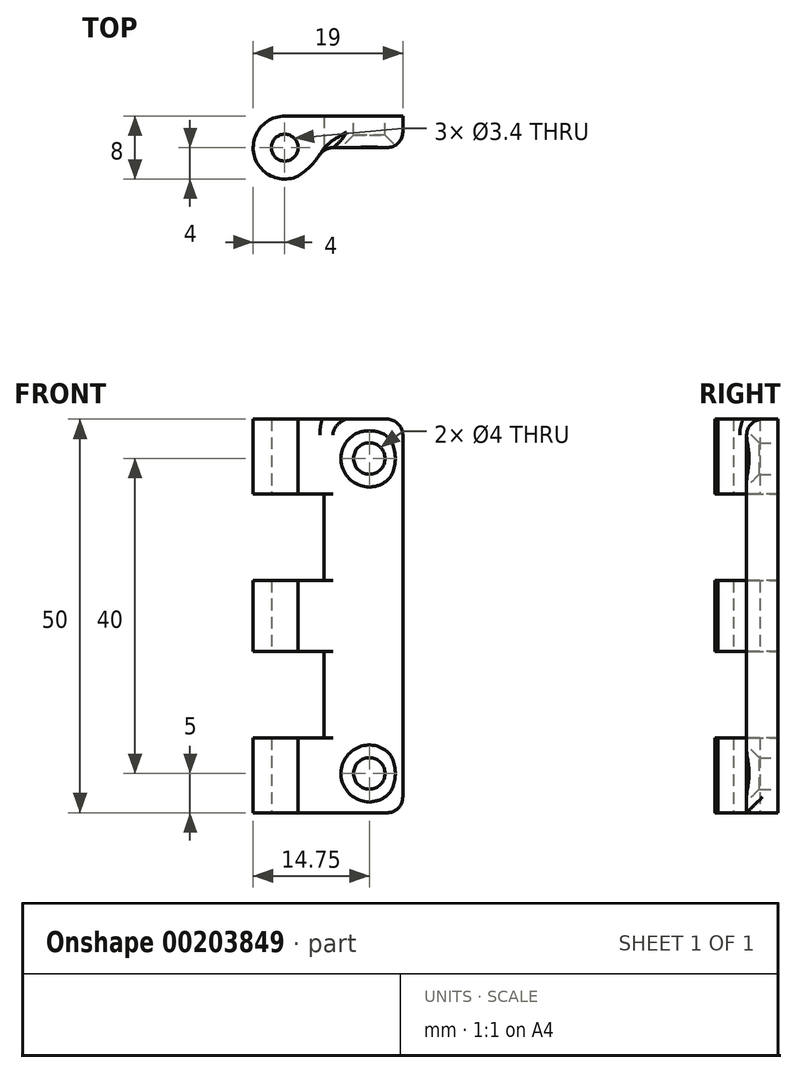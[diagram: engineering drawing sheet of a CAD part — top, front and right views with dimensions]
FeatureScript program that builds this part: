
annotation { "Feature Type Name" : "Feature", "Feature Type Description" : "" }
export const myFeature = defineFeature(function(context is Context, id is Id, definition is map)
    precondition{}
    {
        {
            var Q0;
            Q0=qCreatedBy(makeId("Front.planeOp"),FACE);
            var sketch = newSketch(context, id + "F0", { "sketchPlane" : qUnion([Q0])});
            skLineSegment(sketch, "E0", {"start": v(0, -25) * mm, "end": v(0, 25) * mm});
            skLineSegment(sketch, "E1", {"start": v(0, 25) * mm, "end": v(15, 25) * mm});
            skLineSegment(sketch, "E2", {"start": v(15, 25) * mm, "end": v(15, -25) * mm});
            skLineSegment(sketch, "E3", {"start": v(15, -25) * mm, "end": v(0, -25) * mm});
            skCircle(sketch, "E4", {"center": v(10.75, 20) * mm, "radius": 2 * mm});
            skCircle(sketch, "E5", {"center": v(10.75, -20) * mm, "radius": 2 * mm});
            skLineSegment(sketch, "E6", {"start": v(10.75, -20) * mm, "end": v(10.75, 20) * mm, "construction": true});
            skSolve(sketch);
        }
        {
            var Q0;
            Q0 = qSketchRegion(id + "F0", true);
            extrude(context, id + "F1", {"entities" : qUnion([Q0]), "endBound" : BoundingType.SYMMETRIC, "depth" : 4 * mm});
        }
        {
            var Q0;
            Q0=makeQuery(id+"F1.opExtrude","SWEPT_FACE",FACE,{"disambiguationData":[OSD([sQuery(id+"F0.wireOp",EDGE,"E3")])]});
            var sketch = newSketch(context, id + "F2", { "sketchPlane" : qUnion([Q0])});
            skArc(sketch, "E7", {"start": v(2, 5.46) * mm, "mid": v(-3.46, 0) * mm, "end": v(4, 2) * mm});
            skLineSegment(sketch, "E8", {"start": v(2, 5.46) * mm, "end": v(8, 2) * mm});
            skLineSegment(sketch, "E9", {"start": v(8, 2) * mm, "end": v(4, 2) * mm});
            skSolve(sketch);
        }
        {
            var Q0;
            Q0 = qSketchRegion(id + "F2", true);
            extrude(context, id + "F3", {"entities" : qUnion([Q0]), "operationType" : NewBodyOperationType.ADD, "oppositeDirection" : true, "depth" : 50 * mm});
        }
        {
            var Q0;
            Q0=makeQuery(id+"F3.boolean.opBoolean","MERGE",FACE,{"derivedFrom":[makeQuery(id+"F1.opExtrude","SWEPT_FACE",FACE,{"disambiguationData":[OSD([sQuery(id+"F0.wireOp",EDGE,"E3")])]}),makeQuery(id+"F3.opExtrude","CAP_FACE",FACE,{"disambiguationData":[OSD([sQuery(id+"F2.wireOp",EDGE,"E7"),sQuery(id+"F2.wireOp",EDGE,"E8"),sQuery(id+"F2.wireOp",EDGE,"E9")])],"isStart":true})]});
            var sketch = newSketch(context, id + "F4", { "sketchPlane" : qUnion([Q0])});
            skLineSegment(sketch, "E10.bottom", {"start": v(15, 2) * mm, "end": v(5, 2) * mm});
            skLineSegment(sketch, "E10.top", {"start": v(15, 4) * mm, "end": v(5, 4) * mm});
            skLineSegment(sketch, "E10.left", {"start": v(15, 2) * mm, "end": v(15, 4) * mm});
            skLineSegment(sketch, "E10.right", {"start": v(5, 2) * mm, "end": v(5, 4) * mm});
            skSolve(sketch);
        }
        {
            var Q0;
            Q0 = qSketchRegion(id + "F4", true);
            extrude(context, id + "F5", {"entities" : qUnion([Q0]), "operationType" : NewBodyOperationType.REMOVE, "endBound" : BoundingType.THROUGH_ALL, "oppositeDirection" : true, "depth" : 25 * mm});
        }
        {
            var Q0;
            Q0=makeQuery(id+"F5.boolean.opBoolean","MERGE",FACE,{"derivedFrom":[makeQuery(id+"F1.opExtrude","CAP_FACE",FACE,{"disambiguationData":[OSD([sQuery(id+"F0.wireOp",EDGE,"E0"),sQuery(id+"F0.wireOp",EDGE,"E1"),sQuery(id+"F0.wireOp",EDGE,"E2"),sQuery(id+"F0.wireOp",EDGE,"E3")])],"isStart":false}),makeQuery(id+"F5.opExtrude","SWEPT_FACE",FACE,{"disambiguationData":[OSD([sQuery(id+"F4.wireOp",EDGE,"E10.bottom")])]})]});
            var sketch = newSketch(context, id + "F6", { "sketchPlane" : qUnion([Q0])});
            skLineSegment(sketch, "E11.bottom", {"start": v(-5, 15.5) * mm, "end": v(5, 15.5) * mm});
            skLineSegment(sketch, "E11.top", {"start": v(-5, 4.5) * mm, "end": v(5, 4.5) * mm});
            skLineSegment(sketch, "E11.left", {"start": v(-5, 15.5) * mm, "end": v(-5, 4.5) * mm});
            skLineSegment(sketch, "E11.right", {"start": v(5, 15.5) * mm, "end": v(5, 4.5) * mm});
            skLineSegment(sketch, "E12.bottom", {"start": v(-5, -4.5) * mm, "end": v(5, -4.5) * mm});
            skLineSegment(sketch, "E12.top", {"start": v(-5, -15.5) * mm, "end": v(5, -15.5) * mm});
            skLineSegment(sketch, "E12.left", {"start": v(-5, -4.5) * mm, "end": v(-5, -15.5) * mm});
            skLineSegment(sketch, "E12.right", {"start": v(5, -4.5) * mm, "end": v(5, -15.5) * mm});
            skSolve(sketch);
        }
        {
            var Q0;
            Q0 = qSketchRegion(id + "F6", true);
            extrude(context, id + "F7", {"entities" : qUnion([Q0]), "operationType" : NewBodyOperationType.REMOVE, "endBound" : BoundingType.SYMMETRIC, "oppositeDirection" : true, "depth" : 25 * mm});
        }
        {
            var Q0;
            {var subQ0=makeQuery(id+"F5.opExtrude","SWEPT_FACE",FACE,{"disambiguationData":[OSD([sQuery(id+"F4.wireOp",EDGE,"E10.right")])]});var subQ1=sQuery(id+"F2.wireOp",EDGE,"E8");var subQ2=makeQuery(id+"F3.opExtrude","SWEPT_FACE",FACE,{"disambiguationData":[OSD([subQ1])]});Q0=makeQuery(id+"F7.boolean.opBoolean","SPLIT",EDGE,{"disambiguationData":[TD([makeQuery(id+"F1.opExtrude","SWEPT_FACE",FACE,{"disambiguationData":[OSD([sQuery(id+"F0.wireOp",EDGE,"E3")])]})])],"derivedFrom":makeQuery(id+"F5.boolean.opBoolean","INTERSECT",EDGE,{"derivedFrom":[subQ2,subQ0]})});}
            var Q1;
            {var subQ0=makeQuery(id+"F3.opExtrude","SWEPT_FACE",FACE,{"disambiguationData":[OSD([sQuery(id+"F2.wireOp",EDGE,"E8")])]});var subQ1=makeQuery(id+"F5.opExtrude","SWEPT_FACE",FACE,{"disambiguationData":[OSD([sQuery(id+"F4.wireOp",EDGE,"E10.right")])]});Q1=makeQuery(id+"F7.boolean.opBoolean","SPLIT",EDGE,{"disambiguationData":[TD([makeQuery(id+"F7.opExtrude","SWEPT_FACE",FACE,{"disambiguationData":[OSD([sQuery(id+"F6.wireOp",EDGE,"E11.top")])]})])],"derivedFrom":makeQuery(id+"F5.boolean.opBoolean","INTERSECT",EDGE,{"derivedFrom":[subQ0,subQ1]})});}
            var Q2;
            {var subQ0=makeQuery(id+"F5.opExtrude","SWEPT_FACE",FACE,{"disambiguationData":[OSD([sQuery(id+"F4.wireOp",EDGE,"E10.right")])]});var subQ1=sQuery(id+"F2.wireOp",EDGE,"E8");var subQ2=makeQuery(id+"F3.opExtrude","SWEPT_FACE",FACE,{"disambiguationData":[OSD([subQ1])]});Q2=makeQuery(id+"F7.boolean.opBoolean","SPLIT",EDGE,{"disambiguationData":[TD([makeQuery(id+"F1.opExtrude","SWEPT_FACE",FACE,{"disambiguationData":[OSD([sQuery(id+"F0.wireOp",EDGE,"E1")])]})])],"derivedFrom":makeQuery(id+"F5.boolean.opBoolean","INTERSECT",EDGE,{"derivedFrom":[subQ2,subQ0]})});}
            fillet(context, id + "F8", {"entities" : qUnion([Q0, Q1, Q2]), "radius" : 10 * mm, "tangentPropagation" : true, "allowEdgeOverflow" : false});
        }
        {
            var Q0;
            Q0=makeQuery(id+"F1.opExtrude","CAP_EDGE",EDGE,{"disambiguationData":[OSD([sQuery(id+"F0.wireOp",EDGE,"E2")])],"isStart":false});
            var Q1;
            Q1=makeQuery(id+"F5.boolean.opBoolean","INTERSECT",EDGE,{"derivedFrom":[makeQuery(id+"F3.boolean.opBoolean","MERGE",FACE,{"derivedFrom":[makeQuery(id+"F1.opExtrude","SWEPT_FACE",FACE,{"disambiguationData":[OSD([sQuery(id+"F0.wireOp",EDGE,"E1")])]}),makeQuery(id+"F3.opExtrude","CAP_FACE",FACE,{"disambiguationData":[OSD([sQuery(id+"F2.wireOp",EDGE,"E7"),sQuery(id+"F2.wireOp",EDGE,"E8"),sQuery(id+"F2.wireOp",EDGE,"E9")])],"isStart":false})]}),makeQuery(id+"F5.opExtrude","SWEPT_FACE",FACE,{"disambiguationData":[OSD([sQuery(id+"F4.wireOp",EDGE,"E10.bottom")])]})]});
            var Q2;
            {var subQ0=sQuery(id+"F4.wireOp",EDGE,"E10.right");var subQ1=sQuery(id+"F4.wireOp",EDGE,"E10.bottom");Q2=makeQuery(id+"F7.boolean.opBoolean","SPLIT",EDGE,{"disambiguationData":[TD([makeQuery(id+"F1.opExtrude","CAP_FACE",FACE,{"disambiguationData":[OSD([sQuery(id+"F0.wireOp",EDGE,"E0"),sQuery(id+"F0.wireOp",EDGE,"E1"),sQuery(id+"F0.wireOp",EDGE,"E2"),sQuery(id+"F0.wireOp",EDGE,"E3")])],"isStart":false}),makeQuery(id+"F5.opExtrude","SWEPT_FACE",FACE,{"disambiguationData":[OSD([subQ1])]}),makeQuery(id+"F5.boolean.opBoolean","COPY",FACE,{"derivedFrom":makeQuery(id+"F5.opExtrude","SWEPT_FACE",FACE,{"disambiguationData":[OSD([subQ0])]})}),makeQuery(id+"F7.opExtrude","SWEPT_FACE",FACE,{"disambiguationData":[OSD([sQuery(id+"F6.wireOp",EDGE,"E12.bottom")])]}),makeQuery(id+"F7.opExtrude","SWEPT_FACE",FACE,{"disambiguationData":[OSD([sQuery(id+"F6.wireOp",EDGE,"E12.top")])]}),makeQuery(id+"F7.opExtrude","SWEPT_FACE",FACE,{"disambiguationData":[OSD([sQuery(id+"F6.wireOp",EDGE,"E12.right")])]})])],"derivedFrom":makeQuery(id+"F5.boolean.opBoolean","COPY",EDGE,{"derivedFrom":makeQuery(id+"F5.opExtrude","SWEPT_EDGE",EDGE,{"disambiguationData":[OSD([subQ1,subQ0])]})})});}
            var Q3;
            {var subQ0=sQuery(id+"F4.wireOp",EDGE,"E10.right");var subQ1=sQuery(id+"F4.wireOp",EDGE,"E10.bottom");Q3=makeQuery(id+"F7.boolean.opBoolean","SPLIT",EDGE,{"disambiguationData":[TD([makeQuery(id+"F1.opExtrude","CAP_FACE",FACE,{"disambiguationData":[OSD([sQuery(id+"F0.wireOp",EDGE,"E0"),sQuery(id+"F0.wireOp",EDGE,"E1"),sQuery(id+"F0.wireOp",EDGE,"E2"),sQuery(id+"F0.wireOp",EDGE,"E3")])],"isStart":false}),makeQuery(id+"F5.opExtrude","SWEPT_FACE",FACE,{"disambiguationData":[OSD([subQ1])]}),makeQuery(id+"F5.boolean.opBoolean","COPY",FACE,{"derivedFrom":makeQuery(id+"F5.opExtrude","SWEPT_FACE",FACE,{"disambiguationData":[OSD([subQ0])]})}),makeQuery(id+"F7.opExtrude","SWEPT_FACE",FACE,{"disambiguationData":[OSD([sQuery(id+"F6.wireOp",EDGE,"E11.bottom")])]}),makeQuery(id+"F7.opExtrude","SWEPT_FACE",FACE,{"disambiguationData":[OSD([sQuery(id+"F6.wireOp",EDGE,"E11.top")])]}),makeQuery(id+"F7.opExtrude","SWEPT_FACE",FACE,{"disambiguationData":[OSD([sQuery(id+"F6.wireOp",EDGE,"E11.right")])]})])],"derivedFrom":makeQuery(id+"F5.boolean.opBoolean","COPY",EDGE,{"derivedFrom":makeQuery(id+"F5.opExtrude","SWEPT_EDGE",EDGE,{"disambiguationData":[OSD([subQ1,subQ0])]})})});}
            var Q4;
            Q4=makeQuery(id+"F5.boolean.opBoolean","MERGE",EDGE,{"derivedFrom":[makeQuery(id+"F1.opExtrude","CAP_EDGE",EDGE,{"disambiguationData":[OSD([sQuery(id+"F0.wireOp",EDGE,"E3")])],"isStart":false}),makeQuery(id+"F5.opExtrude","CAP_EDGE",EDGE,{"disambiguationData":[OSD([sQuery(id+"F4.wireOp",EDGE,"E10.bottom")])],"isStart":true})]});
            var Q5;
            Q5=makeQuery(id+"F1.opExtrude","SWEPT_EDGE",EDGE,{"disambiguationData":[OSD([sQuery(id+"F0.wireOp",EDGE,"E2"),sQuery(id+"F0.wireOp",EDGE,"E3")])]});
            var Q6;
            Q6=makeQuery(id+"F1.opExtrude","SWEPT_EDGE",EDGE,{"disambiguationData":[OSD([sQuery(id+"F0.wireOp",EDGE,"E1"),sQuery(id+"F0.wireOp",EDGE,"E2")])]});
            fillet(context, id + "F9", {"entities" : qUnion([Q0, Q1, Q2, Q3, Q4, Q5, Q6]), "radius" : 2 * mm, "tangentPropagation" : true, "allowEdgeOverflow" : false});
        }
        {
            var Q0;
            {var subQ0=sQuery(id+"F0.wireOp",EDGE,"E3");var subQ1=makeQuery(id+"F5.opExtrude","SWEPT_FACE",FACE,{"disambiguationData":[OSD([sQuery(id+"F4.wireOp",EDGE,"E10.right")])]});var subQ2=sQuery(id+"F2.wireOp",EDGE,"E8");var subQ3=makeQuery(id+"F3.opExtrude","SWEPT_FACE",FACE,{"disambiguationData":[OSD([subQ2])]});Q0=makeQuery(id+"F8.opFillet","BLEND_EDGE",EDGE,{"blendedFrom":[makeQuery(id+"F7.boolean.opBoolean","SPLIT",EDGE,{"disambiguationData":[TD([makeQuery(id+"F1.opExtrude","SWEPT_FACE",FACE,{"disambiguationData":[OSD([subQ0])]})])],"derivedFrom":makeQuery(id+"F5.boolean.opBoolean","INTERSECT",EDGE,{"derivedFrom":[subQ3,subQ1]})}),makeQuery(id+"F5.boolean.opBoolean","MERGE",FACE,{"derivedFrom":[makeQuery(id+"F1.opExtrude","CAP_FACE",FACE,{"disambiguationData":[OSD([sQuery(id+"F0.wireOp",EDGE,"E0"),sQuery(id+"F0.wireOp",EDGE,"E1"),sQuery(id+"F0.wireOp",EDGE,"E2"),subQ0])],"isStart":false}),makeQuery(id+"F5.opExtrude","SWEPT_FACE",FACE,{"disambiguationData":[OSD([sQuery(id+"F4.wireOp",EDGE,"E10.bottom")])]})]})],"blendedInto":[makeQuery(id+"F5.boolean.opBoolean","MERGE",FACE,{"derivedFrom":[makeQuery(id+"F1.opExtrude","CAP_FACE",FACE,{"disambiguationData":[OSD([sQuery(id+"F0.wireOp",EDGE,"E0"),sQuery(id+"F0.wireOp",EDGE,"E1"),sQuery(id+"F0.wireOp",EDGE,"E2"),subQ0])],"isStart":false}),makeQuery(id+"F5.opExtrude","SWEPT_FACE",FACE,{"disambiguationData":[OSD([sQuery(id+"F4.wireOp",EDGE,"E10.bottom")])]})]})]});}
            var Q1;
            {var subQ0=makeQuery(id+"F3.opExtrude","SWEPT_FACE",FACE,{"disambiguationData":[OSD([sQuery(id+"F2.wireOp",EDGE,"E8")])]});var subQ1=makeQuery(id+"F5.opExtrude","SWEPT_FACE",FACE,{"disambiguationData":[OSD([sQuery(id+"F4.wireOp",EDGE,"E10.right")])]});Q1=makeQuery(id+"F8.opFillet","BLEND_EDGE",EDGE,{"blendedFrom":[makeQuery(id+"F7.boolean.opBoolean","SPLIT",EDGE,{"disambiguationData":[TD([makeQuery(id+"F7.opExtrude","SWEPT_FACE",FACE,{"disambiguationData":[OSD([sQuery(id+"F6.wireOp",EDGE,"E11.top")])]})])],"derivedFrom":makeQuery(id+"F5.boolean.opBoolean","INTERSECT",EDGE,{"derivedFrom":[subQ0,subQ1]})}),makeQuery(id+"F5.boolean.opBoolean","MERGE",FACE,{"derivedFrom":[makeQuery(id+"F1.opExtrude","CAP_FACE",FACE,{"disambiguationData":[OSD([sQuery(id+"F0.wireOp",EDGE,"E0"),sQuery(id+"F0.wireOp",EDGE,"E1"),sQuery(id+"F0.wireOp",EDGE,"E2"),sQuery(id+"F0.wireOp",EDGE,"E3")])],"isStart":false}),makeQuery(id+"F5.opExtrude","SWEPT_FACE",FACE,{"disambiguationData":[OSD([sQuery(id+"F4.wireOp",EDGE,"E10.bottom")])]})]})],"blendedInto":[makeQuery(id+"F5.boolean.opBoolean","MERGE",FACE,{"derivedFrom":[makeQuery(id+"F1.opExtrude","CAP_FACE",FACE,{"disambiguationData":[OSD([sQuery(id+"F0.wireOp",EDGE,"E0"),sQuery(id+"F0.wireOp",EDGE,"E1"),sQuery(id+"F0.wireOp",EDGE,"E2"),sQuery(id+"F0.wireOp",EDGE,"E3")])],"isStart":false}),makeQuery(id+"F5.opExtrude","SWEPT_FACE",FACE,{"disambiguationData":[OSD([sQuery(id+"F4.wireOp",EDGE,"E10.bottom")])]})]})]});}
            var Q2;
            {var subQ0=sQuery(id+"F0.wireOp",EDGE,"E1");var subQ1=makeQuery(id+"F5.opExtrude","SWEPT_FACE",FACE,{"disambiguationData":[OSD([sQuery(id+"F4.wireOp",EDGE,"E10.right")])]});var subQ2=sQuery(id+"F2.wireOp",EDGE,"E8");var subQ3=makeQuery(id+"F3.opExtrude","SWEPT_FACE",FACE,{"disambiguationData":[OSD([subQ2])]});Q2=makeQuery(id+"F8.opFillet","BLEND_EDGE",EDGE,{"blendedFrom":[makeQuery(id+"F7.boolean.opBoolean","SPLIT",EDGE,{"disambiguationData":[TD([makeQuery(id+"F1.opExtrude","SWEPT_FACE",FACE,{"disambiguationData":[OSD([subQ0])]})])],"derivedFrom":makeQuery(id+"F5.boolean.opBoolean","INTERSECT",EDGE,{"derivedFrom":[subQ3,subQ1]})}),makeQuery(id+"F5.boolean.opBoolean","MERGE",FACE,{"derivedFrom":[makeQuery(id+"F1.opExtrude","CAP_FACE",FACE,{"disambiguationData":[OSD([sQuery(id+"F0.wireOp",EDGE,"E0"),subQ0,sQuery(id+"F0.wireOp",EDGE,"E2"),sQuery(id+"F0.wireOp",EDGE,"E3")])],"isStart":false}),makeQuery(id+"F5.opExtrude","SWEPT_FACE",FACE,{"disambiguationData":[OSD([sQuery(id+"F4.wireOp",EDGE,"E10.bottom")])]})]})],"blendedInto":[makeQuery(id+"F5.boolean.opBoolean","MERGE",FACE,{"derivedFrom":[makeQuery(id+"F1.opExtrude","CAP_FACE",FACE,{"disambiguationData":[OSD([sQuery(id+"F0.wireOp",EDGE,"E0"),subQ0,sQuery(id+"F0.wireOp",EDGE,"E2"),sQuery(id+"F0.wireOp",EDGE,"E3")])],"isStart":false}),makeQuery(id+"F5.opExtrude","SWEPT_FACE",FACE,{"disambiguationData":[OSD([sQuery(id+"F4.wireOp",EDGE,"E10.bottom")])]})]})]});}
            var Q3;
            {var subQ0=sQuery(id+"F4.wireOp",EDGE,"E10.right");var subQ1=makeQuery(id+"F5.opExtrude","SWEPT_FACE",FACE,{"disambiguationData":[OSD([subQ0])]});var subQ2=sQuery(id+"F2.wireOp",EDGE,"E8");var subQ3=makeQuery(id+"F3.opExtrude","SWEPT_FACE",FACE,{"disambiguationData":[OSD([subQ2])]});var subQ4=makeQuery(id+"F3.opExtrude","CAP_FACE",FACE,{"disambiguationData":[OSD([sQuery(id+"F2.wireOp",EDGE,"E7"),subQ2,sQuery(id+"F2.wireOp",EDGE,"E9")])],"isStart":false});var subQ5=makeQuery(id+"F1.opExtrude","SWEPT_FACE",FACE,{"disambiguationData":[OSD([sQuery(id+"F0.wireOp",EDGE,"E1")])]});Q3=makeQuery(id+"F9.opFillet","BLEND_EDGE",EDGE,{"blendedFrom":[makeQuery(id+"F5.boolean.opBoolean","INTERSECT",EDGE,{"derivedFrom":[makeQuery(id+"F3.boolean.opBoolean","MERGE",FACE,{"derivedFrom":[subQ5,subQ4]}),makeQuery(id+"F5.opExtrude","SWEPT_FACE",FACE,{"disambiguationData":[OSD([sQuery(id+"F4.wireOp",EDGE,"E10.bottom")])]})]}),makeQuery(id+"F8.opFillet","BLEND_FACE",FACE,{"disambiguationData":[OSD([subQ2,subQ0]),TDD([makeQuery(id+"F7.boolean.opBoolean","SPLIT",EDGE,{"disambiguationData":[TD([subQ5])],"derivedFrom":makeQuery(id+"F5.boolean.opBoolean","INTERSECT",EDGE,{"derivedFrom":[subQ3,subQ1]})})])]})],"blendedInto":[makeQuery(id+"F8.opFillet","BLEND_FACE",FACE,{"disambiguationData":[OSD([subQ2,subQ0]),TDD([makeQuery(id+"F7.boolean.opBoolean","SPLIT",EDGE,{"disambiguationData":[TD([subQ5])],"derivedFrom":makeQuery(id+"F5.boolean.opBoolean","INTERSECT",EDGE,{"derivedFrom":[subQ3,subQ1]})})])]})]});}
            fillet(context, id + "F10", {"entities" : qUnion([Q0, Q1, Q2, Q3]), "radius" : 2 * mm, "tangentPropagation" : true, "allowEdgeOverflow" : false});
        }
        {
            var Q0;
            Q0=makeQuery(id+"F3.boolean.opBoolean","MERGE",FACE,{"derivedFrom":[makeQuery(id+"F1.opExtrude","SWEPT_FACE",FACE,{"disambiguationData":[OSD([sQuery(id+"F0.wireOp",EDGE,"E3")])]}),makeQuery(id+"F3.opExtrude","CAP_FACE",FACE,{"disambiguationData":[OSD([sQuery(id+"F2.wireOp",EDGE,"E7"),sQuery(id+"F2.wireOp",EDGE,"E8"),sQuery(id+"F2.wireOp",EDGE,"E9")])],"isStart":true})]});
            var sketch = newSketch(context, id + "F11", { "sketchPlane" : qUnion([Q0])});
            skLineSegment(sketch, "E13", {"start": v(0, 6) * mm, "end": v(0, 2) * mm, "construction": true});
            skCircle(sketch, "E14", {"center": v(0, 2) * mm, "radius": 1.7 * mm});
            skSolve(sketch);
        }
        {
            var Q0;
            Q0 = qSketchRegion(id + "F11", true);
            extrude(context, id + "F12", {"entities" : qUnion([Q0]), "operationType" : NewBodyOperationType.REMOVE, "endBound" : BoundingType.THROUGH_ALL, "oppositeDirection" : true, "depth" : 25 * mm});
        }
        {
            var Q0;
            Q0=makeQuery(id+"F1.opExtrude","CAP_EDGE",EDGE,{"disambiguationData":[OSD([sQuery(id+"F0.wireOp",EDGE,"E4")])],"isStart":false});
            var Q1;
            Q1=makeQuery(id+"F1.opExtrude","CAP_EDGE",EDGE,{"disambiguationData":[OSD([sQuery(id+"F0.wireOp",EDGE,"E5")])],"isStart":false});
            chamfer(context, id + "F13", {"entities" : qUnion([Q0, Q1]), "width" : 1.6 * mm, "tangentPropagation" : true});
        }
    });
